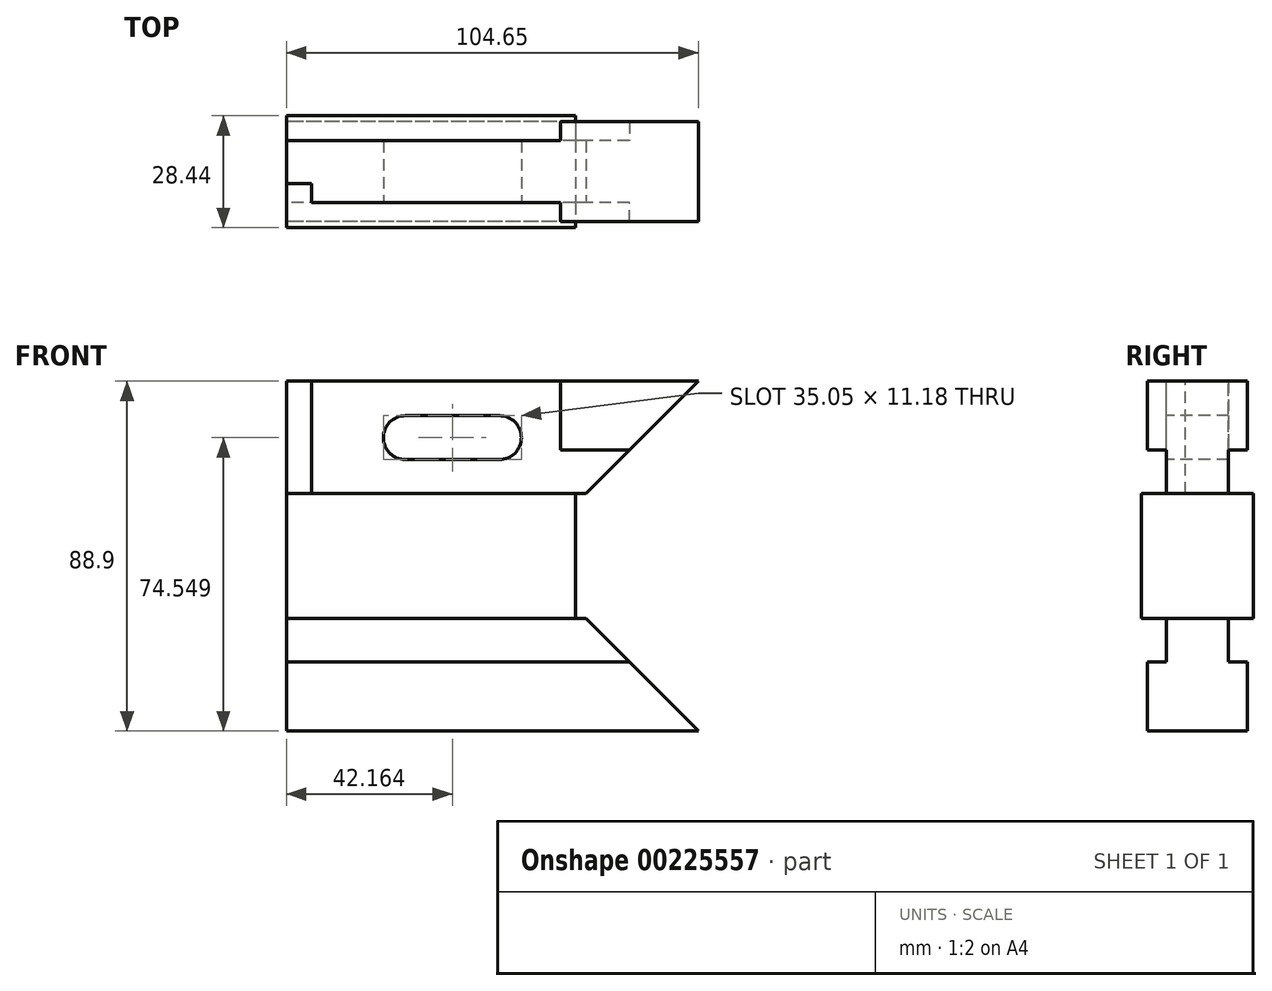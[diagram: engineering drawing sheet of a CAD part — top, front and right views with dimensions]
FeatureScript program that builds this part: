
annotation { "Feature Type Name" : "Feature", "Feature Type Description" : "" }
export const myFeature = defineFeature(function(context is Context, id is Id, definition is map)
    precondition{}
    {
        {
            var Q0;
            Q0=qCreatedBy(makeId("Right.planeOp"),FACE);
            var sketch = newSketch(context, id + "F0", { "sketchPlane" : qUnion([Q0])});
            skLineSegment(sketch, "E0", {"start": v(0, 44.45) * mm, "end": v(0, -47.4) * mm, "construction": true});
            skLineSegment(sketch, "E1", {"start": v(0, 44.45) * mm, "end": v(12.7, 44.45) * mm});
            skLineSegment(sketch, "E2", {"start": v(12.7, 44.45) * mm, "end": v(12.7, 26.92) * mm});
            skLineSegment(sketch, "E3", {"start": v(12.7, 26.92) * mm, "end": v(7.87, 26.92) * mm});
            skLineSegment(sketch, "E4", {"start": v(7.87, 26.92) * mm, "end": v(7.87, 15.88) * mm});
            skLineSegment(sketch, "E5", {"start": v(7.87, 15.88) * mm, "end": v(14.22, 15.88) * mm});
            skLineSegment(sketch, "E6", {"start": v(14.22, 15.88) * mm, "end": v(14.22, 0) * mm});
            skLineSegment(sketch, "E7", {"start": v(0, 0) * mm, "end": v(26.63, 0) * mm, "construction": true});
            skLineSegment(sketch, "E8.MirrorCS", {"start": v(0, -44.45) * mm, "end": v(12.7, -44.45) * mm});
            skLineSegment(sketch, "E9.MirrorCS", {"start": v(12.7, -44.45) * mm, "end": v(12.7, -26.92) * mm});
            skLineSegment(sketch, "E10.MirrorCS", {"start": v(12.7, -26.92) * mm, "end": v(7.87, -26.92) * mm});
            skLineSegment(sketch, "E11.MirrorCS", {"start": v(7.87, -26.92) * mm, "end": v(7.87, -15.88) * mm});
            skLineSegment(sketch, "E12.MirrorCS", {"start": v(7.87, -15.88) * mm, "end": v(14.22, -15.88) * mm});
            skLineSegment(sketch, "E13.MirrorCS", {"start": v(14.22, -15.88) * mm, "end": v(14.22, 0) * mm});
            skLineSegment(sketch, "E14.MirrorCS", {"start": v(-12.7, -26.92) * mm, "end": v(-7.87, -26.92) * mm});
            skLineSegment(sketch, "E15.MirrorCS", {"start": v(-12.7, 26.92) * mm, "end": v(-7.87, 26.92) * mm});
            skLineSegment(sketch, "E16.MirrorCS", {"start": v(0, 44.45) * mm, "end": v(-12.7, 44.45) * mm});
            skLineSegment(sketch, "E17.MirrorCS", {"start": v(-14.22, -15.88) * mm, "end": v(-14.22, 0) * mm});
            skLineSegment(sketch, "E18.MirrorCS", {"start": v(-12.7, 44.45) * mm, "end": v(-12.7, 26.92) * mm});
            skLineSegment(sketch, "E19.MirrorCS", {"start": v(-7.87, -26.92) * mm, "end": v(-7.87, -15.88) * mm});
            skLineSegment(sketch, "E20.MirrorCS", {"start": v(-7.87, -15.88) * mm, "end": v(-14.22, -15.88) * mm});
            skLineSegment(sketch, "E21.MirrorCS", {"start": v(-12.7, -44.45) * mm, "end": v(-12.7, -26.92) * mm});
            skLineSegment(sketch, "E22.MirrorCS", {"start": v(-14.22, 15.88) * mm, "end": v(-14.22, 0) * mm});
            skLineSegment(sketch, "E23.MirrorCS", {"start": v(-7.87, 15.88) * mm, "end": v(-14.22, 15.88) * mm});
            skLineSegment(sketch, "E24.MirrorCS", {"start": v(0, -44.45) * mm, "end": v(-12.7, -44.45) * mm});
            skLineSegment(sketch, "E25.MirrorCS", {"start": v(-7.87, 26.92) * mm, "end": v(-7.87, 15.88) * mm});
            skSolve(sketch);
        }
        {
            var Q0;
            Q0 = qSketchRegion(id + "F0", true);
            extrude(context, id + "F1", {"entities" : qUnion([Q0]), "depth" : 104.65 * mm});
        }
        {
            var Q0;
            Q0=makeQuery(id+"F1.opExtrude","SWEPT_FACE",FACE,{"disambiguationData":[OSD([sQuery(id+"F0.wireOp",EDGE,"E17.MirrorCS"),sQuery(id+"F0.wireOp",EDGE,"E22.MirrorCS")])]});
            var sketch = newSketch(context, id + "F2", { "sketchPlane" : qUnion([Q0])});
            skLineSegment(sketch, "E26", {"start": v(0, 0) * mm, "end": v(146.66, 0) * mm, "construction": true});
            skLineSegment(sketch, "E27", {"start": v(73.4, 0) * mm, "end": v(73.4, 15.87) * mm});
            skLineSegment(sketch, "E28", {"start": v(73.4, 15.87) * mm, "end": v(76.07, 15.87) * mm});
            skLineSegment(sketch, "E29", {"start": v(104.65, 15.87) * mm, "end": v(104.65, 0) * mm});
            skLineSegment(sketch, "E30", {"start": v(104.65, 15.87) * mm, "end": v(104.65, 44.45) * mm});
            skLineSegment(sketch, "E31", {"start": v(76.07, 15.87) * mm, "end": v(104.65, 44.45) * mm});
            skLineSegment(sketch, "E32.MirrorCS", {"start": v(73.4, -15.87) * mm, "end": v(76.07, -15.87) * mm});
            skLineSegment(sketch, "E33.MirrorCS", {"start": v(104.65, -15.87) * mm, "end": v(104.65, -44.45) * mm});
            skLineSegment(sketch, "E34.MirrorCS", {"start": v(76.07, -15.87) * mm, "end": v(104.65, -44.45) * mm});
            skLineSegment(sketch, "E35.MirrorCS", {"start": v(73.4, 0) * mm, "end": v(73.4, -15.87) * mm});
            skLineSegment(sketch, "E36.MirrorCS", {"start": v(104.65, -15.87) * mm, "end": v(104.65, 0) * mm});
            skSolve(sketch);
        }
        {
            var Q0;
            Q0 = qSketchRegion(id + "F2", true);
            extrude(context, id + "F3", {"entities" : qUnion([Q0]), "operationType" : NewBodyOperationType.REMOVE, "endBound" : BoundingType.THROUGH_ALL, "oppositeDirection" : true, "depth" : 25.4 * mm});
        }
        {
            var Q0;
            Q0=makeQuery(id+"F1.opExtrude","SWEPT_FACE",FACE,{"disambiguationData":[OSD([sQuery(id+"F0.wireOp",EDGE,"E1"),sQuery(id+"F0.wireOp",EDGE,"E16.MirrorCS")])]});
            cPlane(context, id + "F4", {"entities" : qUnion([Q0]), "cplaneType" : CPlaneType.OFFSET, "offset" : 44.45 * mm, "oppositeDirection" : true, "width" : 152.4 * mm, "height" : 152.4 * mm});
        }
        {
            var Q0;
            Q0=makeQuery(id+"F1.opExtrude","SWEPT_FACE",FACE,{"disambiguationData":[OSD([sQuery(id+"F0.wireOp",EDGE,"E1"),sQuery(id+"F0.wireOp",EDGE,"E16.MirrorCS")])]});
            var sketch = newSketch(context, id + "F5", { "sketchPlane" : qUnion([Q0])});
            skLineSegment(sketch, "E37.bottom", {"start": v(0, 12.7) * mm, "end": v(69.6, 12.7) * mm});
            skLineSegment(sketch, "E37.top", {"start": v(0, 7.87) * mm, "end": v(69.6, 7.87) * mm});
            skLineSegment(sketch, "E37.left", {"start": v(0, 12.7) * mm, "end": v(0, 7.87) * mm});
            skLineSegment(sketch, "E37.right", {"start": v(69.6, 12.7) * mm, "end": v(69.6, 7.87) * mm});
            skLineSegment(sketch, "E38", {"start": v(0, 0) * mm, "end": v(86.93, 0) * mm, "construction": true});
            skLineSegment(sketch, "E39.MirrorCS", {"start": v(0, -12.7) * mm, "end": v(69.6, -12.7) * mm});
            skLineSegment(sketch, "E40.MirrorCS", {"start": v(6.35, -7.87) * mm, "end": v(69.6, -7.87) * mm});
            skLineSegment(sketch, "E41.MirrorCS", {"start": v(69.6, -12.7) * mm, "end": v(69.6, -7.87) * mm});
            skLineSegment(sketch, "E42", {"start": v(0, -3.05) * mm, "end": v(6.35, -3.05) * mm});
            skLineSegment(sketch, "E43", {"start": v(6.35, -3.05) * mm, "end": v(6.35, -7.87) * mm});
            skLineSegment(sketch, "E44", {"start": v(0, -3.05) * mm, "end": v(0, -12.7) * mm});
            skSolve(sketch);
        }
        {
            var Q0;
            Q0 = qSketchRegion(id + "F5", true);
            extrude(context, id + "F6", {"entities" : qUnion([Q0]), "operationType" : NewBodyOperationType.REMOVE, "oppositeDirection" : true, "depth" : 28.57 * mm});
        }
        {
            var Q0;
            Q0=makeQuery(id+"F6.boolean.opBoolean","MERGE",FACE,{"derivedFrom":[makeQuery(id+"F1.opExtrude","SWEPT_FACE",FACE,{"disambiguationData":[OSD([sQuery(id+"F0.wireOp",EDGE,"E25.MirrorCS")])]}),makeQuery(id+"F6.opExtrude","SWEPT_FACE",FACE,{"disambiguationData":[OSD([sQuery(id+"F5.wireOp",EDGE,"E40.MirrorCS")])]})]});
            var sketch = newSketch(context, id + "F7", { "sketchPlane" : qUnion([Q0])});
            skArc(sketch, "E45", {"start": v(30.23, 35.69) * mm, "mid": v(24.64, 30.1) * mm, "end": v(30.23, 24.51) * mm});
            skLineSegment(sketch, "E46", {"start": v(30.23, 30.1) * mm, "end": v(42.16, 30.1) * mm, "construction": true});
            skLineSegment(sketch, "E47", {"start": v(30.23, 35.69) * mm, "end": v(42.16, 35.69) * mm});
            skLineSegment(sketch, "E48.MirrorCS", {"start": v(30.23, 24.51) * mm, "end": v(42.16, 24.51) * mm});
            skLineSegment(sketch, "E49", {"start": v(42.16, 35.69) * mm, "end": v(42.16, 24.51) * mm, "construction": true});
            skLineSegment(sketch, "E50.MirrorCS", {"start": v(54.1, 30.1) * mm, "end": v(42.16, 30.1) * mm, "construction": true});
            skArc(sketch, "E51.MirrorCS", {"start": v(54.1, 35.69) * mm, "mid": v(59.7, 30.1) * mm, "end": v(54.1, 24.51) * mm});
            skLineSegment(sketch, "E52.MirrorCS", {"start": v(54.1, 35.69) * mm, "end": v(42.16, 35.69) * mm});
            skLineSegment(sketch, "E53.MirrorCS", {"start": v(54.1, 24.51) * mm, "end": v(42.16, 24.51) * mm});
            skSolve(sketch);
        }
        {
            var Q0;
            Q0=makeQuery(id+"F7.imprint","IMPRINT",FACE,{"disambiguationData":[TD([[makeQuery(id+"F7.imprint","IMPRINT",EDGE,{"derivedFrom":sQuery(id+"F7.wireOp",EDGE,"E45")}),1.0]])]});
            extrude(context, id + "F8", {"entities" : qUnion([Q0]), "operationType" : NewBodyOperationType.REMOVE, "endBound" : BoundingType.THROUGH_ALL, "oppositeDirection" : true, "depth" : 25.4 * mm});
        }
    });
